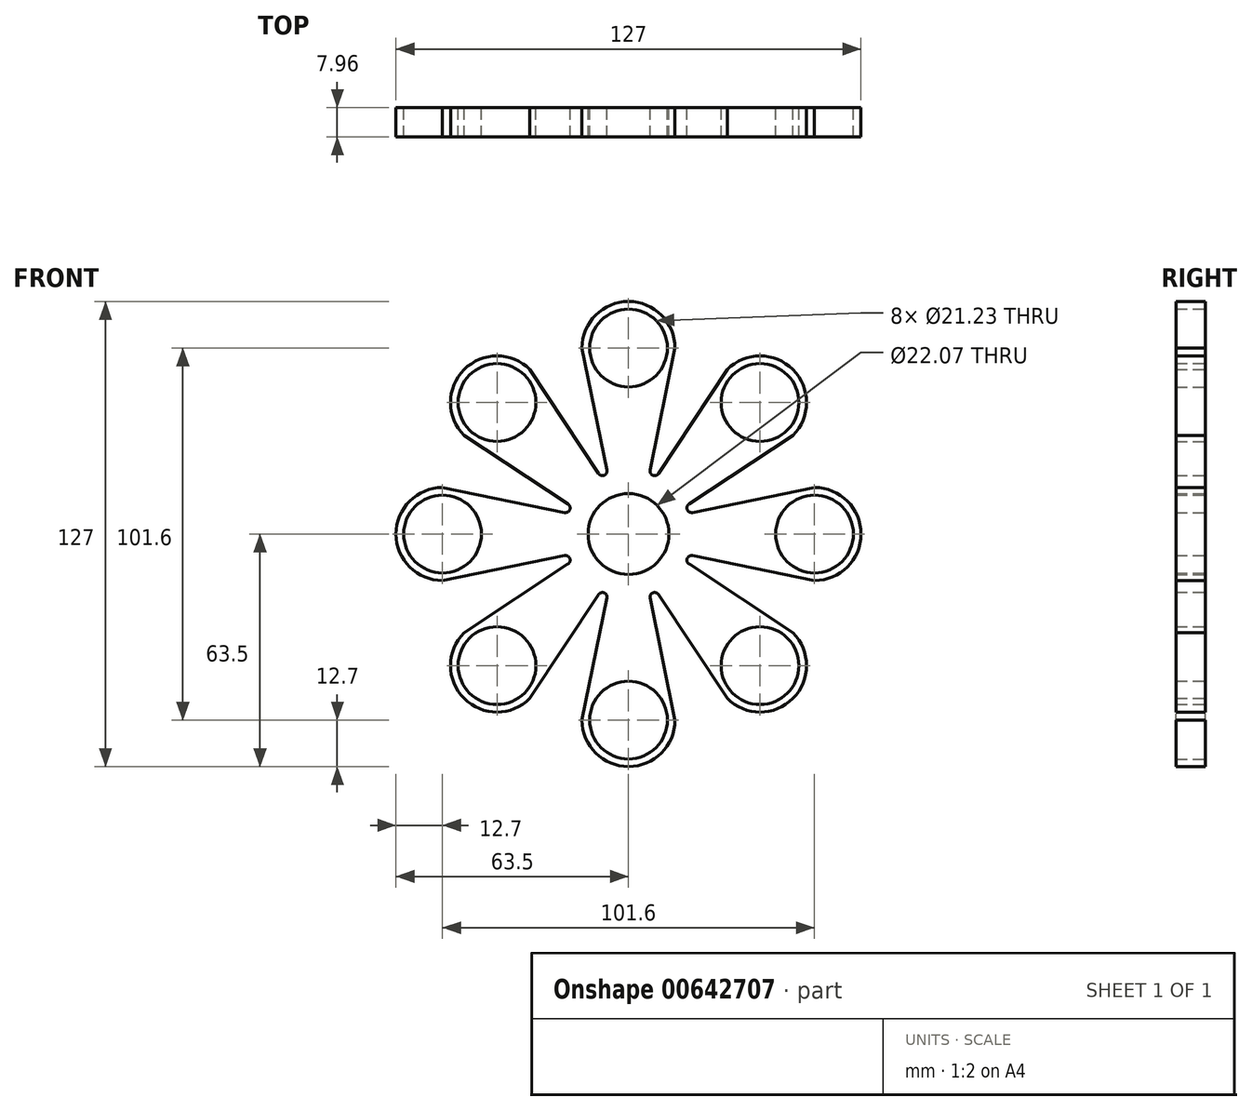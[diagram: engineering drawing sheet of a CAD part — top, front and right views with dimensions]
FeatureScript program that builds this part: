
annotation { "Feature Type Name" : "Feature", "Feature Type Description" : "" }
export const myFeature = defineFeature(function(context is Context, id is Id, definition is map)
    precondition{}
    {
        {
            var Q0;
            Q0=qCreatedBy(makeId("Front.planeOp"),FACE);
            var sketch = newSketch(context, id + "F0", { "sketchPlane" : qUnion([Q0])});
            skCircle(sketch, "E0", {"center": v(0, 0) * mm, "radius": 11.04 * mm});
            skLineSegment(sketch, "E1", {"start": v(0, 0) * mm, "end": v(-50.8, 0) * mm, "construction": true});
            skCircle(sketch, "E2", {"center": v(-50.8, 0) * mm, "radius": 10.62 * mm});
            skCircle(sketch, "E3.cCircle", {"center": v(0, 0) * mm, "radius": 11.04 * mm, "construction": true});
            skLineSegment(sketch, "E3.0", {"start": v(-4.57, 11.04) * mm, "end": v(4.57, 11.04) * mm});
            skLineSegment(sketch, "E3.1", {"start": v(4.57, 11.04) * mm, "end": v(11.04, 4.57) * mm});
            skLineSegment(sketch, "E3.2", {"start": v(11.04, 4.57) * mm, "end": v(11.04, -4.57) * mm});
            skLineSegment(sketch, "E3.3", {"start": v(11.04, -4.57) * mm, "end": v(4.57, -11.04) * mm});
            skLineSegment(sketch, "E3.4", {"start": v(4.57, -11.04) * mm, "end": v(-4.57, -11.04) * mm});
            skLineSegment(sketch, "E3.5", {"start": v(-4.57, -11.04) * mm, "end": v(-11.04, -4.57) * mm});
            skLineSegment(sketch, "E3.6", {"start": v(-11.04, -4.57) * mm, "end": v(-11.04, 4.57) * mm});
            skLineSegment(sketch, "E3.7", {"start": v(-11.04, 4.57) * mm, "end": v(-4.57, 11.04) * mm});
            skPoint(sketch, "E3.0.midPoint", {"position": v(0, 11.04) * mm});
            skArc(sketch, "E4", {"start": v(-50.8, 12.7) * mm, "mid": v(-63.5, 0) * mm, "end": v(-50.8, -12.7) * mm});
            skLineSegment(sketch, "E5", {"start": v(-50.8, 12.7) * mm, "end": v(-11.04, 4.57) * mm});
            skLineSegment(sketch, "E6", {"start": v(-50.8, -12.7) * mm, "end": v(-11.04, -4.57) * mm});
            skLineSegment(sketch, "E7.MirrorCS", {"start": v(50.8, 12.7) * mm, "end": v(11.04, 4.57) * mm});
            skArc(sketch, "E8.MirrorCS", {"start": v(50.8, 12.7) * mm, "mid": v(63.5, 0) * mm, "end": v(50.8, -12.7) * mm});
            skLineSegment(sketch, "E9.MirrorCS", {"start": v(50.8, -12.7) * mm, "end": v(11.04, -4.57) * mm});
            skCircle(sketch, "E10.MirrorC", {"center": v(50.8, 0) * mm, "radius": 10.62 * mm});
            skLineSegment(sketch, "E11", {"start": v(0, 0) * mm, "end": v(0, -50.8) * mm, "construction": true});
            skCircle(sketch, "E12", {"center": v(0, -50.8) * mm, "radius": 10.62 * mm});
            skArc(sketch, "E13", {"start": v(12.7, -50.8) * mm, "mid": v(0, -63.5) * mm, "end": v(-12.7, -50.8) * mm});
            skLineSegment(sketch, "E14", {"start": v(12.7, -50.8) * mm, "end": v(4.57, -11.04) * mm});
            skLineSegment(sketch, "E15", {"start": v(-12.7, -50.8) * mm, "end": v(-4.57, -11.04) * mm});
            skLineSegment(sketch, "E16.MirrorCS", {"start": v(12.7, 50.8) * mm, "end": v(4.57, 11.04) * mm});
            skLineSegment(sketch, "E17.MirrorCS", {"start": v(-12.7, 50.8) * mm, "end": v(-4.57, 11.04) * mm});
            skCircle(sketch, "E18.MirrorC", {"center": v(0, 50.8) * mm, "radius": 10.62 * mm});
            skArc(sketch, "E19.MirrorCS", {"start": v(12.7, 50.8) * mm, "mid": v(0, 63.5) * mm, "end": v(-12.7, 50.8) * mm});
            skLineSegment(sketch, "E20", {"start": v(0, 0) * mm, "end": v(-35.92, -35.92) * mm, "construction": true});
            skCircle(sketch, "E21", {"center": v(-35.92, -35.92) * mm, "radius": 10.62 * mm});
            skLineSegment(sketch, "E22", {"start": v(-35.92, -35.92) * mm, "end": v(-26.94, -44.9) * mm, "construction": true});
            skLineSegment(sketch, "E23", {"start": v(-35.92, -35.92) * mm, "end": v(-44.9, -26.94) * mm, "construction": true});
            skArc(sketch, "E24", {"start": v(-44.9, -26.94) * mm, "mid": v(-44.9, -44.9) * mm, "end": v(-26.94, -44.9) * mm});
            skLineSegment(sketch, "E25", {"start": v(-44.9, -26.94) * mm, "end": v(-11.04, -4.57) * mm});
            skLineSegment(sketch, "E26", {"start": v(-26.94, -44.9) * mm, "end": v(-4.57, -11.04) * mm});
            skLineSegment(sketch, "E27.MirrorCS", {"start": v(-44.9, 26.94) * mm, "end": v(-11.04, 4.57) * mm});
            skArc(sketch, "E28.MirrorCS", {"start": v(-44.9, 26.94) * mm, "mid": v(-44.9, 44.9) * mm, "end": v(-26.94, 44.9) * mm});
            skCircle(sketch, "E29.MirrorC", {"center": v(-35.92, 35.92) * mm, "radius": 10.62 * mm});
            skLineSegment(sketch, "E30.MirrorCS", {"start": v(-26.94, 44.9) * mm, "end": v(-4.57, 11.04) * mm});
            skLineSegment(sketch, "E31.MirrorCS", {"start": v(26.94, -44.9) * mm, "end": v(4.57, -11.04) * mm});
            skArc(sketch, "E32.MirrorCS", {"start": v(44.9, -26.94) * mm, "mid": v(44.9, -44.9) * mm, "end": v(26.94, -44.9) * mm});
            skLineSegment(sketch, "E33.MirrorCS", {"start": v(44.9, -26.94) * mm, "end": v(11.04, -4.57) * mm});
            skCircle(sketch, "E34.MirrorC", {"center": v(35.92, -35.92) * mm, "radius": 10.62 * mm});
            skLineSegment(sketch, "E35.MirrorCS", {"start": v(26.94, 44.9) * mm, "end": v(4.57, 11.04) * mm});
            skArc(sketch, "E36.MirrorCS", {"start": v(44.9, 26.94) * mm, "mid": v(44.9, 44.9) * mm, "end": v(26.94, 44.9) * mm});
            skCircle(sketch, "E37.MirrorC", {"center": v(35.92, 35.92) * mm, "radius": 10.62 * mm});
            skLineSegment(sketch, "E38.MirrorCS", {"start": v(44.9, 26.94) * mm, "end": v(11.04, 4.57) * mm});
            skSolve(sketch);
        }
        {
            var Q0;
            Q0 = qSketchRegion(id + "F0", true);
            extrude(context, id + "F1", {"entities" : qUnion([Q0]), "endBound" : BoundingType.SYMMETRIC, "depth" : 7.95 * mm, "offsetDistance" : 25.4 * mm});
        }
        {
            var Q0;
            Q0=makeQuery(id+"F1.opExtrude","SWEPT_EDGE",EDGE,{"disambiguationData":[OSD([sQuery(id+"F0.wireOp",EDGE,"E3.0"),sQuery(id+"F0.wireOp",EDGE,"E3.1"),sQuery(id+"F0.wireOp",EDGE,"E16.MirrorCS"),sQuery(id+"F0.wireOp",EDGE,"E35.MirrorCS")])]});
            var Q1;
            Q1=makeQuery(id+"F1.opExtrude","SWEPT_EDGE",EDGE,{"disambiguationData":[OSD([sQuery(id+"F0.wireOp",EDGE,"E3.0"),sQuery(id+"F0.wireOp",EDGE,"E3.7"),sQuery(id+"F0.wireOp",EDGE,"E17.MirrorCS"),sQuery(id+"F0.wireOp",EDGE,"E30.MirrorCS")])]});
            var Q2;
            Q2=makeQuery(id+"F1.opExtrude","SWEPT_EDGE",EDGE,{"disambiguationData":[OSD([sQuery(id+"F0.wireOp",EDGE,"E3.6"),sQuery(id+"F0.wireOp",EDGE,"E3.7"),sQuery(id+"F0.wireOp",EDGE,"E5"),sQuery(id+"F0.wireOp",EDGE,"E27.MirrorCS")])]});
            var Q3;
            Q3=makeQuery(id+"F1.opExtrude","SWEPT_EDGE",EDGE,{"disambiguationData":[OSD([sQuery(id+"F0.wireOp",EDGE,"E3.5"),sQuery(id+"F0.wireOp",EDGE,"E3.6"),sQuery(id+"F0.wireOp",EDGE,"E6"),sQuery(id+"F0.wireOp",EDGE,"E25")])]});
            var Q4;
            Q4=makeQuery(id+"F1.opExtrude","SWEPT_EDGE",EDGE,{"disambiguationData":[OSD([sQuery(id+"F0.wireOp",EDGE,"E3.4"),sQuery(id+"F0.wireOp",EDGE,"E3.5"),sQuery(id+"F0.wireOp",EDGE,"E15"),sQuery(id+"F0.wireOp",EDGE,"E26")])]});
            var Q5;
            Q5=makeQuery(id+"F1.opExtrude","SWEPT_EDGE",EDGE,{"disambiguationData":[OSD([sQuery(id+"F0.wireOp",EDGE,"E3.3"),sQuery(id+"F0.wireOp",EDGE,"E3.4"),sQuery(id+"F0.wireOp",EDGE,"E14"),sQuery(id+"F0.wireOp",EDGE,"E31.MirrorCS")])]});
            var Q6;
            Q6=makeQuery(id+"F1.opExtrude","SWEPT_EDGE",EDGE,{"disambiguationData":[OSD([sQuery(id+"F0.wireOp",EDGE,"E3.2"),sQuery(id+"F0.wireOp",EDGE,"E3.3"),sQuery(id+"F0.wireOp",EDGE,"E9.MirrorCS"),sQuery(id+"F0.wireOp",EDGE,"E33.MirrorCS")])]});
            var Q7;
            Q7=makeQuery(id+"F1.opExtrude","SWEPT_EDGE",EDGE,{"disambiguationData":[OSD([sQuery(id+"F0.wireOp",EDGE,"E3.1"),sQuery(id+"F0.wireOp",EDGE,"E3.2"),sQuery(id+"F0.wireOp",EDGE,"E7.MirrorCS"),sQuery(id+"F0.wireOp",EDGE,"E38.MirrorCS")])]});
            fillet(context, id + "F2", {"entities" : qUnion([Q0, Q1, Q2, Q3, Q4, Q5, Q6, Q7]), "radius" : 1.27 * mm, "tangentPropagation" : true, "allowEdgeOverflow" : false});
        }
    });
